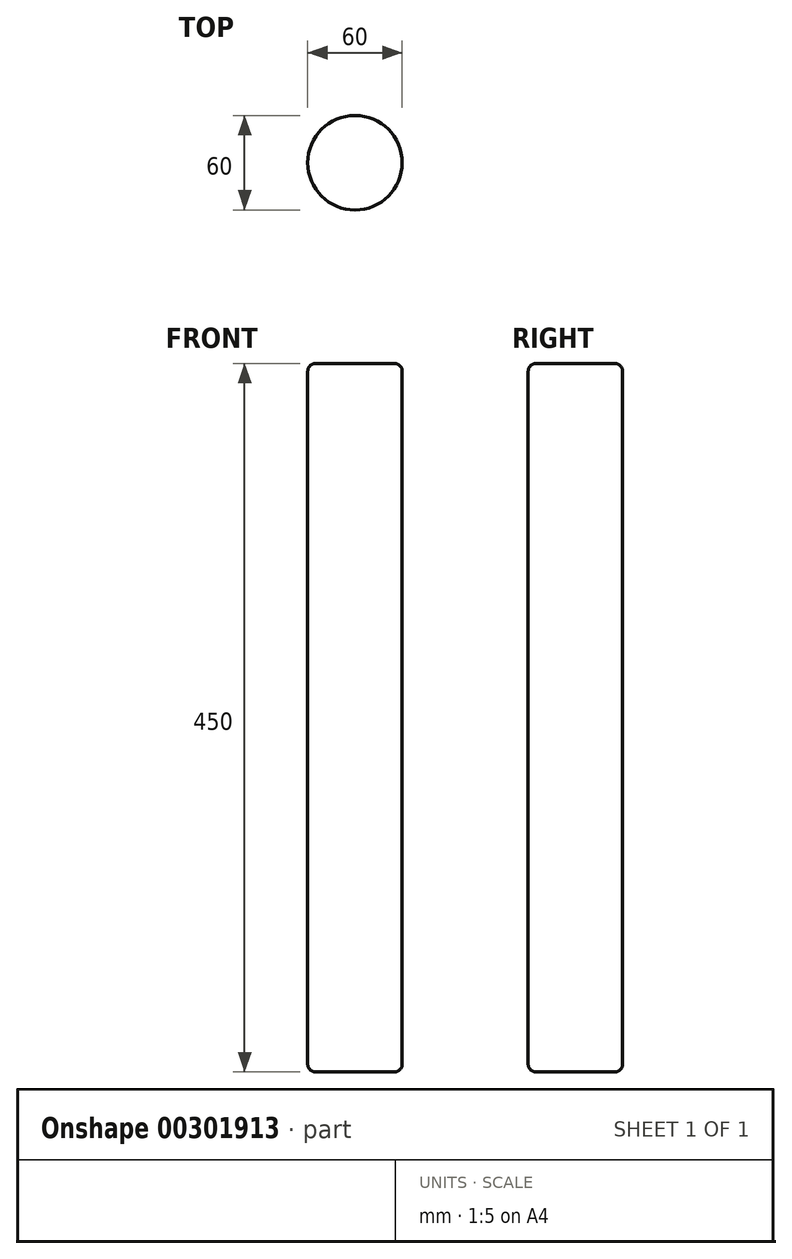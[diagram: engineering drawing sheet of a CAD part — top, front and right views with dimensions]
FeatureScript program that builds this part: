
annotation { "Feature Type Name" : "Feature", "Feature Type Description" : "" }
export const myFeature = defineFeature(function(context is Context, id is Id, definition is map)
    precondition{}
    {
        {
            var Q0;
            Q0=qCreatedBy(makeId("Top.planeOp"),FACE);
            var sketch = newSketch(context, id + "F0", { "sketchPlane" : qUnion([Q0])});
            skCircle(sketch, "E0", {"center": v(0, 0) * mm, "radius": 30 * mm});
            skSolve(sketch);
        }
        {
            var Q0;
            Q0=makeQuery(id+"F0.imprint","IMPRINT",FACE,{"disambiguationData":[TD([[makeQuery(id+"F0.imprint","IMPRINT",EDGE,{"derivedFrom":sQuery(id+"F0.wireOp",EDGE,"E0")}),1.0]])]});
            extrude(context, id + "F1", {"entities" : qUnion([Q0]), "depth" : 450 * mm});
        }
        {
            var Q0;
            Q0=makeQuery(id+"F1.opExtrude","SWEPT_FACE",FACE,{"disambiguationData":[OSD([sQuery(id+"F0.wireOp",EDGE,"E0")])]});
            var Q1;
            Q1=makeQuery(id+"F1.opExtrude","CAP_FACE",FACE,{"disambiguationData":[OSD([sQuery(id+"F0.wireOp",EDGE,"E0")])],"isStart":false});
            var Q2;
            Q2=makeQuery(id+"F1.opExtrude","CAP_FACE",FACE,{"disambiguationData":[OSD([sQuery(id+"F0.wireOp",EDGE,"E0")])],"isStart":true});
            fillet(context, id + "F2", {"entities" : qUnion([Q0, Q1, Q2]), "radius" : 5 * mm, "tangentPropagation" : true, "allowEdgeOverflow" : false});
        }
    });
